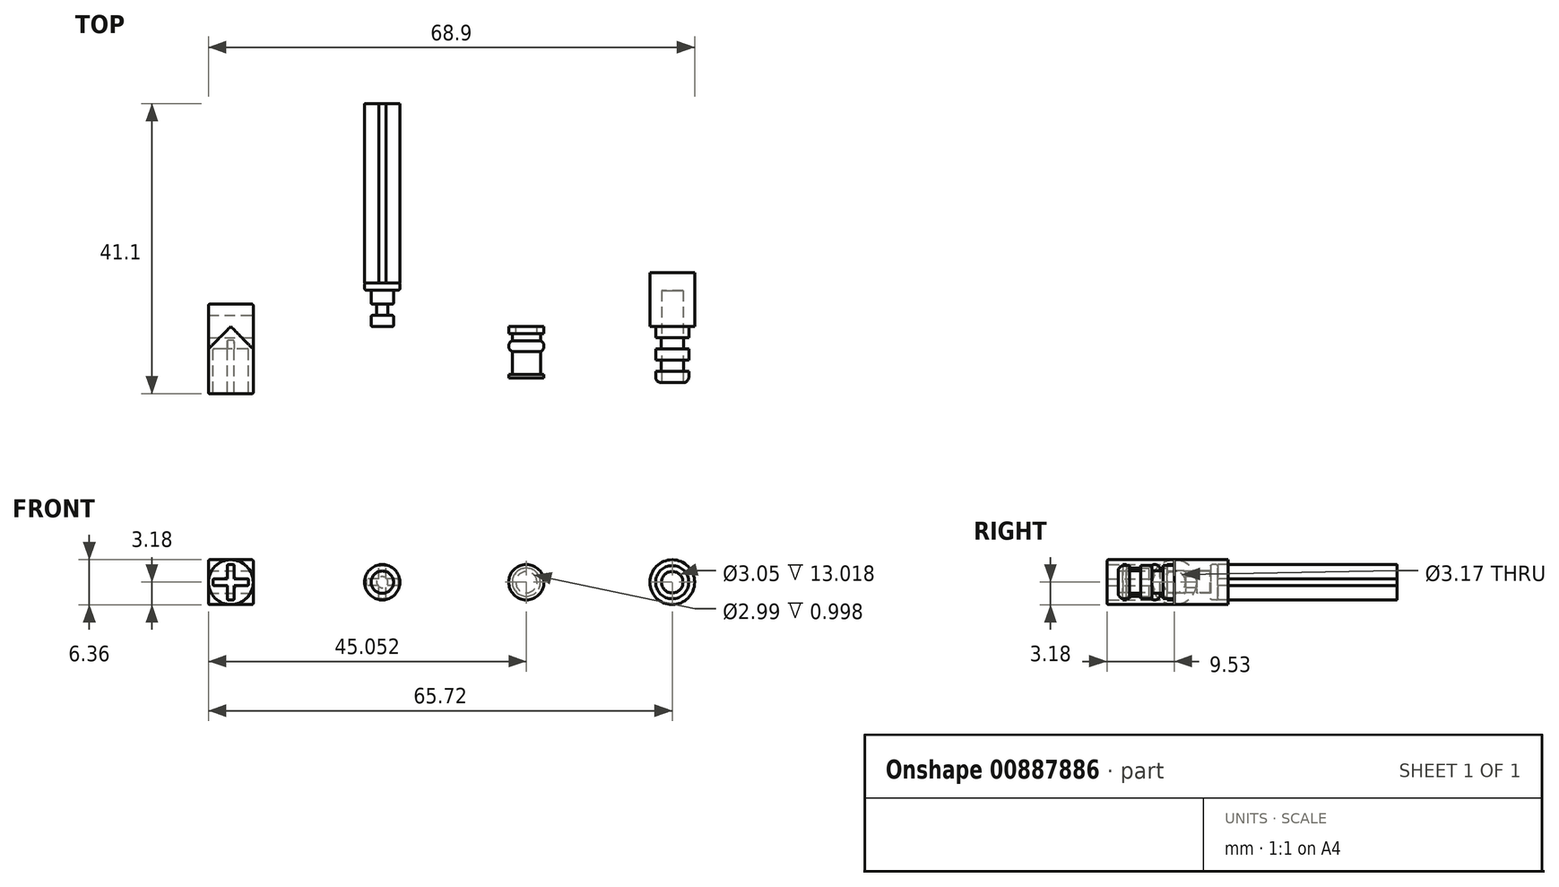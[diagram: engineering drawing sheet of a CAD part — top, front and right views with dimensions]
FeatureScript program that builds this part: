
annotation { "Feature Type Name" : "Feature", "Feature Type Description" : "" }
export const myFeature = defineFeature(function(context is Context, id is Id, definition is map)
    precondition{}
    {
        {
            var Q0;
            Q0=qCreatedBy(makeId("Front.planeOp"),FACE);
            var sketch = newSketch(context, id + "F0", { "sketchPlane" : qUnion([Q0])});
            skCircle(sketch, "E0", {"center": v(-62.55, 0) * mm, "radius": 3.18 * mm});
            skLineSegment(sketch, "E1.bottom", {"start": v(-62.88, 2.5) * mm, "end": v(-62.2, 2.5) * mm});
            skLineSegment(sketch, "E1.top", {"start": v(-62.89, -2.5) * mm, "end": v(-62.2, -2.5) * mm});
            skLineSegment(sketch, "E1.left", {"start": v(-63.05, 2.34) * mm, "end": v(-63.05, -2.34) * mm});
            skLineSegment(sketch, "E1.right", {"start": v(-62.05, 2.34) * mm, "end": v(-62.05, -2.34) * mm});
            skLineSegment(sketch, "E2.bottom", {"start": v(-64.89, 0.5) * mm, "end": v(-60.2, 0.5) * mm});
            skLineSegment(sketch, "E2.top", {"start": v(-64.89, -0.5) * mm, "end": v(-60.2, -0.5) * mm});
            skLineSegment(sketch, "E2.left", {"start": v(-65.05, 0.34) * mm, "end": v(-65.05, -0.34) * mm});
            skLineSegment(sketch, "E2.right", {"start": v(-60.05, 0.34) * mm, "end": v(-60.05, -0.34) * mm});
            skPoint(sketch, "E3.visualSharp", {"position": v(-63.05, 2.5) * mm});
            skArc(sketch, "E3.filletArc", {"start": v(-62.88, 2.5) * mm, "mid": v(-63, 2.45) * mm, "end": v(-63.05, 2.34) * mm});
            skPoint(sketch, "E4.visualSharp", {"position": v(-62.05, 2.5) * mm});
            skArc(sketch, "E4.filletArc", {"start": v(-62.05, 2.34) * mm, "mid": v(-62.1, 2.45) * mm, "end": v(-62.2, 2.5) * mm});
            skPoint(sketch, "E5.visualSharp", {"position": v(-60.05, 0.5) * mm});
            skArc(sketch, "E5.filletArc", {"start": v(-60.05, 0.34) * mm, "mid": v(-60.1, 0.45) * mm, "end": v(-60.2, 0.5) * mm});
            skPoint(sketch, "E6.visualSharp", {"position": v(-60.05, -0.5) * mm});
            skArc(sketch, "E6.filletArc", {"start": v(-60.2, -0.5) * mm, "mid": v(-60.1, -0.45) * mm, "end": v(-60.05, -0.34) * mm});
            skPoint(sketch, "E7.visualSharp", {"position": v(-62.05, -2.5) * mm});
            skArc(sketch, "E7.filletArc", {"start": v(-62.2, -2.5) * mm, "mid": v(-62.1, -2.45) * mm, "end": v(-62.05, -2.34) * mm});
            skPoint(sketch, "E8.visualSharp", {"position": v(-63.05, -2.5) * mm});
            skArc(sketch, "E8.filletArc", {"start": v(-63.05, -2.34) * mm, "mid": v(-63, -2.45) * mm, "end": v(-62.89, -2.5) * mm});
            skPoint(sketch, "E9.visualSharp", {"position": v(-65.05, -0.5) * mm});
            skArc(sketch, "E9.filletArc", {"start": v(-65.05, -0.34) * mm, "mid": v(-65, -0.45) * mm, "end": v(-64.89, -0.5) * mm});
            skPoint(sketch, "E10.visualSharp", {"position": v(-65.05, 0.5) * mm});
            skArc(sketch, "E10.filletArc", {"start": v(-64.89, 0.5) * mm, "mid": v(-65, 0.45) * mm, "end": v(-65.05, 0.34) * mm});
            skLineSegment(sketch, "E11.bottom", {"start": v(-65.72, 3.18) * mm, "end": v(-59.37, 3.18) * mm});
            skLineSegment(sketch, "E11.top", {"start": v(-65.72, 0) * mm, "end": v(-59.37, 0) * mm});
            skLineSegment(sketch, "E11.left", {"start": v(-65.72, 3.18) * mm, "end": v(-65.72, 0) * mm});
            skLineSegment(sketch, "E11.right", {"start": v(-59.37, 3.18) * mm, "end": v(-59.37, 0) * mm});
            skSolve(sketch);
        }
        {
            var Q0;
            Q0=makeQuery(id+"F0.imprint","IMPRINT",FACE,{"disambiguationData":[TD([[makeQuery(id+"F0.imprint","IMPRINT",EDGE,{"derivedFrom":sQuery(id+"F0.wireOp",EDGE,"E1.bottom")}),1.0]])]});
            var Q1;
            Q1=makeQuery(id+"F0.imprint","IMPRINT",FACE,{"disambiguationData":[TD([[makeQuery(id+"F0.imprint","IMPRINT",EDGE,{"derivedFrom":sQuery(id+"F0.wireOp",EDGE,"E1.top")}),-1.0]])]});
            extrude(context, id + "F1", {"entities" : qUnion([Q0, Q1]), "depth" : 9.52 * mm, "offsetDistance" : 25.4 * mm});
        }
        {
            var Q0;
            Q0=makeQuery(id+"F0.imprint","IMPRINT",FACE,{"disambiguationData":[TD([[makeQuery(id+"F0.imprint","IMPRINT",EDGE,{"derivedFrom":sQuery(id+"F0.wireOp",EDGE,"E1.bottom")}),1.0]])]});
            var Q1;
            {var subQ0=sQuery(id+"F0.wireOp",EDGE,"E11.right");Q1=makeQuery(id+"F0.imprint","IMPRINT",FACE,{"disambiguationData":[TD([[makeQuery(id+"F0.imprint","IMPRINT",EDGE,{"derivedFrom":subQ0}),-1.0]])]});}
            var Q2;
            {var subQ0=sQuery(id+"F0.wireOp",EDGE,"E11.left");Q2=makeQuery(id+"F0.imprint","IMPRINT",FACE,{"disambiguationData":[TD([[makeQuery(id+"F0.imprint","IMPRINT",EDGE,{"derivedFrom":subQ0}),1.0]])]});}
            var Q3;
            {var subQ0=sQuery(id+"F0.wireOp",EDGE,"E5.filletArc");Q3=makeQuery(id+"F0.imprint","IMPRINT",FACE,{"disambiguationData":[TD([[makeQuery(id+"F0.imprint","IMPRINT",EDGE,{"derivedFrom":subQ0}),1.0]])]});}
            var Q4;
            {var subQ0=sQuery(id+"F0.wireOp",EDGE,"E2.bottom");var subQ1=sQuery(id+"F0.wireOp",EDGE,"E1.left");var subQ2=makeQuery(id+"F0.imprint","INTERSECT",VERTEX,{"derivedFrom":[subQ1,subQ0]});Q4=makeQuery(id+"F0.imprint","IMPRINT",FACE,{"disambiguationData":[TD([[makeQuery(id+"F0.imprint","IMPRINT",EDGE,{"disambiguationData":[TD([[subQ2,-1.0]])],"derivedFrom":subQ1}),1.0]])]});}
            var Q5;
            {var subQ0=sQuery(id+"F0.wireOp",EDGE,"E10.filletArc");Q5=makeQuery(id+"F0.imprint","IMPRINT",FACE,{"disambiguationData":[TD([[makeQuery(id+"F0.imprint","IMPRINT",EDGE,{"derivedFrom":subQ0}),1.0]])]});}
            var Q6;
            Q6=makeQuery(id+"F0.imprint","IMPRINT",FACE,{"disambiguationData":[TD([[makeQuery(id+"F0.imprint","IMPRINT",EDGE,{"derivedFrom":sQuery(id+"F0.wireOp",EDGE,"E1.bottom")}),-1.0]])]});
            var Q7;
            Q7=sQuery(id+"F0.wireOp",EDGE,"E11.top");
            revolve(context, id + "F2", {"operationType" : NewBodyOperationType.ADD, "surfaceOperationType" : NewSurfaceOperationType.NEW, "entities" : qUnion([Q0, Q1, Q2, Q3, Q4, Q5, Q6]), "axis" : qUnion([Q7]), "revolveType" : RevolveType.FULL});
        }
        {
            var Q0;
            Q0=makeQuery(id+"F2.opRevolve","SWEPT_FACE",FACE,{"disambiguationData":[OSD([sQuery(id+"F0.wireOp",EDGE,"E11.right")])]});
            var sketch = newSketch(context, id + "F3", { "sketchPlane" : qUnion([Q0])});
            skCircle(sketch, "E12", {"center": v(0, 0) * mm, "radius": 1.59 * mm});
            skSolve(sketch);
        }
        {
            var Q0;
            Q0=makeQuery(id+"F3.imprint","IMPRINT",FACE,{"disambiguationData":[TD([[makeQuery(id+"F3.imprint","IMPRINT",EDGE,{"derivedFrom":sQuery(id+"F3.wireOp",EDGE,"E12")}),1.0]])]});
            extrude(context, id + "F4", {"entities" : qUnion([Q0]), "operationType" : NewBodyOperationType.REMOVE, "oppositeDirection" : true, "depth" : 6.35 * mm, "offsetDistance" : 25.4 * mm});
        }
        {
            var Q0;
            Q0=qCreatedBy(makeId("Front.planeOp"),FACE);
            var sketch = newSketch(context, id + "F5", { "sketchPlane" : qUnion([Q0])});
            skCircle(sketch, "E13", {"center": v(-41.08, 0) * mm, "radius": 1.59 * mm});
            skSolve(sketch);
        }
        {
            var Q0;
            Q0=makeQuery(id+"F5.imprint","IMPRINT",FACE,{"disambiguationData":[TD([[makeQuery(id+"F5.imprint","IMPRINT",EDGE,{"derivedFrom":sQuery(id+"F5.wireOp",EDGE,"E13")}),1.0]])]});
            extrude(context, id + "F6", {"entities" : qUnion([Q0]), "depth" : 1.59 * mm, "offsetDistance" : 25.4 * mm});
        }
        {
            var Q0;
            Q0=makeQuery(id+"F6.opExtrude","CAP_FACE",FACE,{"disambiguationData":[OSD([sQuery(id+"F5.wireOp",EDGE,"E13")])],"isStart":false});
            var sketch = newSketch(context, id + "F7", { "sketchPlane" : qUnion([Q0])});
            skCircle(sketch, "E14", {"center": v(-41.08, 0) * mm, "radius": 0.8 * mm});
            skSolve(sketch);
        }
        {
            var Q0;
            Q0=makeQuery(id+"F7.imprint","IMPRINT",FACE,{"disambiguationData":[TD([[makeQuery(id+"F7.imprint","IMPRINT",EDGE,{"derivedFrom":sQuery(id+"F7.wireOp",EDGE,"E14")}),1.0]])]});
            extrude(context, id + "F8", {"entities" : qUnion([Q0]), "operationType" : NewBodyOperationType.ADD, "depth" : 1.59 * mm, "offsetDistance" : 25.4 * mm});
        }
        {
            var Q0;
            Q0=makeQuery(id+"F8.opExtrude","CAP_FACE",FACE,{"disambiguationData":[OSD([sQuery(id+"F7.wireOp",EDGE,"E14")])],"isStart":false});
            var sketch = newSketch(context, id + "F9", { "sketchPlane" : qUnion([Q0])});
            skCircle(sketch, "E15", {"center": v(-41.08, 0) * mm, "radius": 1.59 * mm});
            skSolve(sketch);
        }
        {
            var Q0;
            Q0=makeQuery(id+"F9.imprint","IMPRINT",FACE,{"disambiguationData":[TD([[makeQuery(id+"F9.imprint","IMPRINT",EDGE,{"derivedFrom":makeQuery(id+"F8.opExtrude","CAP_EDGE",EDGE,{"disambiguationData":[OSD([sQuery(id+"F7.wireOp",EDGE,"E14")])],"isStart":false})}),1.0]])]});
            var Q1;
            Q1=makeQuery(id+"F9.imprint","IMPRINT",FACE,{"disambiguationData":[TD([[makeQuery(id+"F9.imprint","IMPRINT",EDGE,{"derivedFrom":sQuery(id+"F9.wireOp",EDGE,"E15")}),1.0]])]});
            extrude(context, id + "F10", {"entities" : qUnion([Q0, Q1]), "operationType" : NewBodyOperationType.ADD, "depth" : 2 * mm, "offsetDistance" : 25.4 * mm});
        }
        {
            var Q0;
            Q0=makeQuery(id+"F10.opExtrude","CAP_FACE",FACE,{"disambiguationData":[OSD([sQuery(id+"F9.wireOp",EDGE,"E15")])],"isStart":false});
            var sketch = newSketch(context, id + "F11", { "sketchPlane" : qUnion([Q0])});
            skCircle(sketch, "E16", {"center": v(-41.08, 0) * mm, "radius": 2.5 * mm});
            skSolve(sketch);
        }
        {
            var Q0;
            Q0=makeQuery(id+"F11.imprint","IMPRINT",FACE,{"disambiguationData":[TD([[makeQuery(id+"F11.imprint","IMPRINT",EDGE,{"derivedFrom":makeQuery(id+"F10.opExtrude","CAP_EDGE",EDGE,{"disambiguationData":[OSD([sQuery(id+"F9.wireOp",EDGE,"E15")])],"isStart":false})}),1.0]])]});
            var Q1;
            Q1=makeQuery(id+"F11.imprint","IMPRINT",FACE,{"disambiguationData":[TD([[makeQuery(id+"F11.imprint","IMPRINT",EDGE,{"derivedFrom":sQuery(id+"F11.wireOp",EDGE,"E16")}),1.0]])]});
            extrude(context, id + "F12", {"entities" : qUnion([Q0, Q1]), "operationType" : NewBodyOperationType.ADD, "depth" : 1 * mm, "offsetDistance" : 25.4 * mm});
        }
        {
            var Q0;
            Q0=makeQuery(id+"F1.opExtrude","CAP_EDGE",EDGE,{"disambiguationData":[OSD([sQuery(id+"F0.wireOp",EDGE,"E0")])],"isStart":false});
            var Q1;
            Q1=makeQuery(id+"F2.opRevolve","SWEPT_EDGE",EDGE,{"disambiguationData":[OSD([sQuery(id+"F0.wireOp",EDGE,"E11.bottom"),sQuery(id+"F0.wireOp",EDGE,"E11.right")])]});
            var Q2;
            Q2=makeQuery(id+"F2.opRevolve","SWEPT_EDGE",EDGE,{"disambiguationData":[OSD([sQuery(id+"F0.wireOp",EDGE,"E11.bottom"),sQuery(id+"F0.wireOp",EDGE,"E11.left")])]});
            var Q3;
            Q3=makeQuery(id+"F6.opExtrude","CAP_EDGE",EDGE,{"disambiguationData":[OSD([sQuery(id+"F5.wireOp",EDGE,"E13")])],"isStart":true});
            var Q4;
            Q4=makeQuery(id+"F6.opExtrude","CAP_EDGE",EDGE,{"disambiguationData":[OSD([sQuery(id+"F5.wireOp",EDGE,"E13")])],"isStart":false});
            var Q5;
            Q5=makeQuery(id+"F4.boolean.opBoolean","COPY",EDGE,{"derivedFrom":makeQuery(id+"F4.opExtrude","CAP_EDGE",EDGE,{"disambiguationData":[OSD([sQuery(id+"F3.wireOp",EDGE,"E12")])],"isStart":true})});
            var Q6;
            Q6=makeQuery(id+"F4.boolean.opBoolean","COPY",EDGE,{"derivedFrom":makeQuery(id+"F4.opExtrude","CAP_EDGE",EDGE,{"disambiguationData":[OSD([sQuery(id+"F3.wireOp",EDGE,"E12")])],"isStart":false})});
            var Q7;
            Q7=makeQuery(id+"F1.opExtrude","CAP_FACE",FACE,{"disambiguationData":[OSD([sQuery(id+"F0.wireOp",EDGE,"E0"),sQuery(id+"F0.wireOp",EDGE,"E1.bottom"),sQuery(id+"F0.wireOp",EDGE,"E1.top"),sQuery(id+"F0.wireOp",EDGE,"E1.left"),sQuery(id+"F0.wireOp",EDGE,"E1.right"),sQuery(id+"F0.wireOp",EDGE,"E2.bottom"),sQuery(id+"F0.wireOp",EDGE,"E2.top"),sQuery(id+"F0.wireOp",EDGE,"E2.left"),sQuery(id+"F0.wireOp",EDGE,"E2.right"),sQuery(id+"F0.wireOp",EDGE,"E3.filletArc"),sQuery(id+"F0.wireOp",EDGE,"E4.filletArc"),sQuery(id+"F0.wireOp",EDGE,"E5.filletArc"),sQuery(id+"F0.wireOp",EDGE,"E6.filletArc"),sQuery(id+"F0.wireOp",EDGE,"E7.filletArc"),sQuery(id+"F0.wireOp",EDGE,"E8.filletArc"),sQuery(id+"F0.wireOp",EDGE,"E9.filletArc"),sQuery(id+"F0.wireOp",EDGE,"E10.filletArc")])],"isStart":false});
            var Q8;
            Q8=makeQuery(id+"F10.opExtrude","CAP_EDGE",EDGE,{"disambiguationData":[OSD([sQuery(id+"F9.wireOp",EDGE,"E15")])],"isStart":true});
            var Q9;
            Q9=makeQuery(id+"F10.opExtrude","CAP_EDGE",EDGE,{"disambiguationData":[OSD([sQuery(id+"F9.wireOp",EDGE,"E15")])],"isStart":false});
            var Q10;
            Q10=makeQuery(id+"F12.opExtrude","CAP_EDGE",EDGE,{"disambiguationData":[OSD([sQuery(id+"F11.wireOp",EDGE,"E16")])],"isStart":true});
            var Q11;
            Q11=makeQuery(id+"F12.opExtrude","CAP_EDGE",EDGE,{"disambiguationData":[OSD([sQuery(id+"F11.wireOp",EDGE,"E16")])],"isStart":false});
            fillet(context, id + "F13", {"entities" : qUnion([Q0, Q1, Q2, Q3, Q4, Q5, Q6, Q7, Q8, Q9, Q10, Q11]), "radius" : 0.2 * mm, "tangentPropagation" : true, "allowEdgeOverflow" : false});
        }
        {
            var Q0;
            Q0=makeQuery(id+"F12.opExtrude","CAP_FACE",FACE,{"disambiguationData":[OSD([sQuery(id+"F11.wireOp",EDGE,"E16")])],"isStart":false});
            var sketch = newSketch(context, id + "F14", { "sketchPlane" : qUnion([Q0])});
            skLineSegment(sketch, "E17.bottom", {"start": v(-40.74, 2.5) * mm, "end": v(-41.42, 2.5) * mm});
            skLineSegment(sketch, "E17.top", {"start": v(-40.74, -2.5) * mm, "end": v(-41.42, -2.5) * mm});
            skLineSegment(sketch, "E17.left", {"start": v(-40.58, 2.34) * mm, "end": v(-40.58, -2.34) * mm});
            skLineSegment(sketch, "E17.right", {"start": v(-41.58, 2.34) * mm, "end": v(-41.58, -2.34) * mm});
            skPoint(sketch, "E17.middle", {"position": v(-41.08, 0) * mm});
            skLineSegment(sketch, "E18.bottom", {"start": v(-38.74, 0.5) * mm, "end": v(-43.41, 0.5) * mm});
            skLineSegment(sketch, "E18.top", {"start": v(-38.74, -0.5) * mm, "end": v(-43.41, -0.5) * mm});
            skLineSegment(sketch, "E18.left", {"start": v(-38.58, 0.34) * mm, "end": v(-38.58, -0.34) * mm});
            skLineSegment(sketch, "E18.right", {"start": v(-43.57, 0.34) * mm, "end": v(-43.57, -0.34) * mm});
            skPoint(sketch, "E19.visualSharp", {"position": v(-41.58, 2.5) * mm});
            skArc(sketch, "E19.filletArc", {"start": v(-41.42, 2.5) * mm, "mid": v(-41.53, 2.45) * mm, "end": v(-41.58, 2.34) * mm});
            skPoint(sketch, "E20.visualSharp", {"position": v(-40.58, 2.5) * mm});
            skArc(sketch, "E20.filletArc", {"start": v(-40.58, 2.34) * mm, "mid": v(-40.62, 2.45) * mm, "end": v(-40.74, 2.5) * mm});
            skPoint(sketch, "E21.visualSharp", {"position": v(-38.58, 0.5) * mm});
            skArc(sketch, "E21.filletArc", {"start": v(-38.58, 0.34) * mm, "mid": v(-38.63, 0.45) * mm, "end": v(-38.74, 0.5) * mm});
            skPoint(sketch, "E22.visualSharp", {"position": v(-38.58, -0.5) * mm});
            skArc(sketch, "E22.filletArc", {"start": v(-38.74, -0.5) * mm, "mid": v(-38.63, -0.45) * mm, "end": v(-38.58, -0.34) * mm});
            skPoint(sketch, "E23.visualSharp", {"position": v(-40.58, -2.5) * mm});
            skArc(sketch, "E23.filletArc", {"start": v(-40.74, -2.5) * mm, "mid": v(-40.62, -2.45) * mm, "end": v(-40.58, -2.34) * mm});
            skPoint(sketch, "E24.visualSharp", {"position": v(-41.58, -2.5) * mm});
            skArc(sketch, "E24.filletArc", {"start": v(-41.58, -2.34) * mm, "mid": v(-41.53, -2.45) * mm, "end": v(-41.42, -2.5) * mm});
            skPoint(sketch, "E25.visualSharp", {"position": v(-43.57, 0.5) * mm});
            skArc(sketch, "E25.filletArc", {"start": v(-43.41, 0.5) * mm, "mid": v(-43.53, 0.45) * mm, "end": v(-43.57, 0.34) * mm});
            skPoint(sketch, "E26.visualSharp", {"position": v(-43.57, -0.5) * mm});
            skArc(sketch, "E26.filletArc", {"start": v(-43.57, -0.34) * mm, "mid": v(-43.53, -0.45) * mm, "end": v(-43.41, -0.5) * mm});
            skSolve(sketch);
        }
        {
            var Q0;
            Q0=makeQuery(id+"F14.imprint","IMPRINT",FACE,{"disambiguationData":[TD([[makeQuery(id+"F14.imprint","IMPRINT",EDGE,{"derivedFrom":sQuery(id+"F14.wireOp",EDGE,"E17.bottom")}),1.0]])]});
            var Q1;
            Q1=makeQuery(id+"F14.imprint","IMPRINT",FACE,{"disambiguationData":[TD([[makeQuery(id+"F14.imprint","IMPRINT",EDGE,{"derivedFrom":sQuery(id+"F14.wireOp",EDGE,"E18.left")}),-1.0]])]});
            var Q2;
            Q2=makeQuery(id+"F14.imprint","IMPRINT",FACE,{"disambiguationData":[TD([[makeQuery(id+"F14.imprint","IMPRINT",EDGE,{"derivedFrom":sQuery(id+"F14.wireOp",EDGE,"E17.top")}),-1.0]])]});
            var Q3;
            {var subQ0=sQuery(id+"F14.wireOp",EDGE,"E18.bottom");var subQ1=sQuery(id+"F14.wireOp",EDGE,"E17.left");var subQ2=makeQuery(id+"F14.imprint","INTERSECT",VERTEX,{"derivedFrom":[subQ1,subQ0]});Q3=makeQuery(id+"F14.imprint","IMPRINT",FACE,{"disambiguationData":[TD([[makeQuery(id+"F14.imprint","IMPRINT",EDGE,{"disambiguationData":[TD([[subQ2,-1.0]])],"derivedFrom":subQ1}),1.0]])]});}
            var Q4;
            {var subQ0=sQuery(id+"F14.wireOp",EDGE,"E18.bottom");var subQ1=sQuery(id+"F14.wireOp",EDGE,"E17.left");var subQ2=makeQuery(id+"F14.imprint","INTERSECT",VERTEX,{"derivedFrom":[subQ1,subQ0]});Q4=makeQuery(id+"F14.imprint","IMPRINT",FACE,{"disambiguationData":[TD([[makeQuery(id+"F14.imprint","IMPRINT",EDGE,{"disambiguationData":[TD([[subQ2,-1.0]])],"derivedFrom":subQ1}),-1.0]])]});}
            var Q5;
            {var subQ0=sQuery(id+"F14.wireOp",EDGE,"E18.bottom");var subQ1=sQuery(id+"F14.wireOp",EDGE,"E17.left");var subQ2=makeQuery(id+"F14.imprint","INTERSECT",VERTEX,{"derivedFrom":[subQ1,subQ0]});Q5=makeQuery(id+"F14.imprint","IMPRINT",FACE,{"disambiguationData":[TD([[makeQuery(id+"F14.imprint","IMPRINT",EDGE,{"disambiguationData":[TD([[subQ2,-1.0]])],"derivedFrom":subQ0}),-1.0]])]});}
            var Q6;
            {var subQ0=sQuery(id+"F14.wireOp",EDGE,"E18.top");var subQ1=sQuery(id+"F14.wireOp",EDGE,"E17.left");var subQ2=makeQuery(id+"F14.imprint","INTERSECT",VERTEX,{"derivedFrom":[subQ1,subQ0]});Q6=makeQuery(id+"F14.imprint","IMPRINT",FACE,{"disambiguationData":[TD([[makeQuery(id+"F14.imprint","IMPRINT",EDGE,{"disambiguationData":[TD([[subQ2,-1.0]])],"derivedFrom":subQ0}),1.0]])]});}
            var Q7;
            Q7=makeQuery(id+"F14.imprint","IMPRINT",FACE,{"disambiguationData":[TD([[makeQuery(id+"F14.imprint","IMPRINT",EDGE,{"derivedFrom":sQuery(id+"F14.wireOp",EDGE,"E18.right")}),1.0]])]});
            var Q8;
            {var subQ0=sQuery(id+"F14.wireOp",EDGE,"E18.bottom");var subQ1=sQuery(id+"F14.wireOp",EDGE,"E17.right");var subQ2=makeQuery(id+"F14.imprint","INTERSECT",VERTEX,{"derivedFrom":[subQ1,subQ0]});Q8=makeQuery(id+"F14.imprint","IMPRINT",FACE,{"disambiguationData":[TD([[makeQuery(id+"F14.imprint","IMPRINT",EDGE,{"disambiguationData":[TD([[subQ2,-1.0]])],"derivedFrom":subQ1}),-1.0]])]});}
            extrude(context, id + "F15", {"entities" : qUnion([Q0, Q1, Q2, Q3, Q4, Q5, Q6, Q7, Q8]), "operationType" : NewBodyOperationType.ADD, "depth" : 25.4 * mm, "offsetDistance" : 25.4 * mm});
        }
        {
            var Q0;
            Q0=makeQuery(id+"F6.opExtrude","SWEPT_BODY",BODY,{"disambiguationData":[OSD([sQuery(id+"F5.wireOp",EDGE,"E13")])]});
            var Q1;
            Q1=makeQuery(id+"F4.boolean.opBoolean","COPY",FACE,{"derivedFrom":makeQuery(id+"F4.opExtrude","SWEPT_FACE",FACE,{"disambiguationData":[OSD([sQuery(id+"F3.wireOp",EDGE,"E12")])]})});
            transform(context, id + "F16", {"entities" : qUnion([Q0]), "transformType" : TransformType.ROTATION, "transformAxis" : qUnion([Q1]), "angle" : 180 * degree, "makeCopy" : false});
        }
        {
            var Q0;
            Q0=qCreatedBy(makeId("Front.planeOp"),FACE);
            var sketch = newSketch(context, id + "F17", { "sketchPlane" : qUnion([Q0])});
            skCircle(sketch, "E27", {"center": v(-20.67, 0) * mm, "radius": 2.5 * mm});
            skCircle(sketch, "E28", {"center": v(-20.67, 0) * mm, "radius": 1.5 * mm});
            skSolve(sketch);
        }
        {
            var Q0;
            Q0 = qSketchRegion(id + "F17", true);
            extrude(context, id + "F18", {"entities" : qUnion([Q0]), "depth" : 1 * mm, "offsetDistance" : 25.4 * mm});
        }
        {
            var Q0;
            Q0=makeQuery(id+"F18.opExtrude","CAP_FACE",FACE,{"disambiguationData":[OSD([sQuery(id+"F17.wireOp",EDGE,"E27")])],"isStart":false});
            var sketch = newSketch(context, id + "F19", { "sketchPlane" : qUnion([Q0])});
            skCircle(sketch, "E29", {"center": v(-20.67, 0) * mm, "radius": 2 * mm});
            skSolve(sketch);
        }
        {
            var Q0;
            Q0 = qSketchRegion(id + "F19", true);
            extrude(context, id + "F20", {"entities" : qUnion([Q0]), "operationType" : NewBodyOperationType.ADD, "depth" : 1 * mm, "offsetDistance" : 25.4 * mm});
        }
        {
            var Q0;
            Q0=makeQuery(id+"F20.opExtrude","CAP_FACE",FACE,{"disambiguationData":[OSD([sQuery(id+"F19.wireOp",EDGE,"E29")])],"isStart":false});
            var sketch = newSketch(context, id + "F21", { "sketchPlane" : qUnion([Q0])});
            skCircle(sketch, "E30", {"center": v(-20.67, 0) * mm, "radius": 2.5 * mm});
            skSolve(sketch);
        }
        {
            var Q0;
            Q0 = qSketchRegion(id + "F21", true);
            extrude(context, id + "F22", {"entities" : qUnion([Q0]), "operationType" : NewBodyOperationType.ADD, "depth" : 1.59 * mm, "offsetDistance" : 25.4 * mm});
        }
        {
            var Q0;
            Q0=makeQuery(id+"F22.opExtrude","CAP_EDGE",EDGE,{"disambiguationData":[OSD([sQuery(id+"F21.wireOp",EDGE,"E30")])],"isStart":true});
            var Q1;
            Q1=makeQuery(id+"F22.opExtrude","CAP_EDGE",EDGE,{"disambiguationData":[OSD([sQuery(id+"F21.wireOp",EDGE,"E30")])],"isStart":false});
            fillet(context, id + "F23", {"entities" : qUnion([Q0, Q1]), "radius" : 0.8 * mm, "tangentPropagation" : true, "allowEdgeOverflow" : false});
        }
        {
            var Q0;
            Q0=makeQuery(id+"F22.opExtrude","CAP_FACE",FACE,{"disambiguationData":[OSD([sQuery(id+"F21.wireOp",EDGE,"E30")])],"isStart":false});
            var sketch = newSketch(context, id + "F24", { "sketchPlane" : qUnion([Q0])});
            skCircle(sketch, "E31", {"center": v(-20.67, 0) * mm, "radius": 2 * mm});
            skSolve(sketch);
        }
        {
            var Q0;
            Q0=makeQuery(id+"F24.imprint","IMPRINT",FACE,{"disambiguationData":[TD([[makeQuery(id+"F24.imprint","IMPRINT",EDGE,{"derivedFrom":sQuery(id+"F24.wireOp",EDGE,"E31")}),1.0]])]});
            var Q1;
            {var subQ0=sQuery(id+"F21.wireOp",EDGE,"E30");Q1=makeQuery(id+"F24.imprint","IMPRINT",FACE,{"disambiguationData":[TD([[makeQuery(id+"F24.imprint","IMPRINT",EDGE,{"derivedFrom":makeQuery(id+"F23.opFillet","BLEND_EDGE",EDGE,{"blendedFrom":[makeQuery(id+"F22.opExtrude","CAP_EDGE",EDGE,{"disambiguationData":[OSD([subQ0])],"isStart":false}),makeQuery(id+"F22.opExtrude","CAP_FACE",FACE,{"disambiguationData":[OSD([subQ0])],"isStart":false})],"blendedInto":[makeQuery(id+"F22.opExtrude","CAP_FACE",FACE,{"disambiguationData":[OSD([subQ0])],"isStart":false})]})}),1.0]])]});}
            extrude(context, id + "F25", {"entities" : qUnion([Q0, Q1]), "operationType" : NewBodyOperationType.ADD, "depth" : 3.17 * mm, "offsetDistance" : 25.4 * mm, "hasSecondDirection" : true, "secondDirectionOppositeDirection" : true, "secondDirectionDepth" : 2.54 * mm});
        }
        {
            var Q0;
            Q0=makeQuery(id+"F25.opExtrude","CAP_FACE",FACE,{"disambiguationData":[OSD([sQuery(id+"F24.wireOp",EDGE,"E31")])],"isStart":false});
            var sketch = newSketch(context, id + "F26", { "sketchPlane" : qUnion([Q0])});
            skCircle(sketch, "E32", {"center": v(-20.67, 0) * mm, "radius": 2.5 * mm});
            skSolve(sketch);
        }
        {
            var Q0;
            Q0=makeQuery(id+"F26.imprint","IMPRINT",FACE,{"disambiguationData":[TD([[makeQuery(id+"F26.imprint","IMPRINT",EDGE,{"derivedFrom":sQuery(id+"F26.wireOp",EDGE,"E32")}),1.0]])]});
            var Q1;
            Q1=makeQuery(id+"F26.imprint","IMPRINT",FACE,{"disambiguationData":[TD([[makeQuery(id+"F26.imprint","IMPRINT",EDGE,{"derivedFrom":makeQuery(id+"F25.opExtrude","CAP_EDGE",EDGE,{"disambiguationData":[OSD([sQuery(id+"F24.wireOp",EDGE,"E31")])],"isStart":false})}),1.0]])]});
            extrude(context, id + "F27", {"entities" : qUnion([Q0, Q1]), "operationType" : NewBodyOperationType.ADD, "depth" : 0.5 * mm, "offsetDistance" : 25.4 * mm});
        }
        {
            var Q0;
            Q0=qCreatedBy(makeId("Front.planeOp"),FACE);
            var sketch = newSketch(context, id + "F28", { "sketchPlane" : qUnion([Q0])});
            skCircle(sketch, "E33", {"center": v(0, 0) * mm, "radius": 2.35 * mm});
            skSolve(sketch);
        }
        {
            var Q0;
            Q0=makeQuery(id+"F28.imprint","IMPRINT",FACE,{"disambiguationData":[TD([[makeQuery(id+"F28.imprint","IMPRINT",EDGE,{"derivedFrom":sQuery(id+"F28.wireOp",EDGE,"E33")}),1.0]])]});
            extrude(context, id + "F29", {"entities" : qUnion([Q0]), "depth" : 1.59 * mm, "offsetDistance" : 25.4 * mm});
        }
        {
            var Q0;
            Q0=makeQuery(id+"F29.opExtrude","CAP_FACE",FACE,{"disambiguationData":[OSD([sQuery(id+"F28.wireOp",EDGE,"E33"),sQuery(id+"F28.wireOp",EDGE,"9ddfb91d-996f-495a-b1ff-16b5f034c826")])],"isStart":false});
            var sketch = newSketch(context, id + "F30", { "sketchPlane" : qUnion([Q0])});
            skCircle(sketch, "E34", {"center": v(0, 0) * mm, "radius": 1.59 * mm});
            skSolve(sketch);
        }
        {
            var Q0;
            Q0=makeQuery(id+"F30.imprint","IMPRINT",FACE,{"disambiguationData":[TD([[makeQuery(id+"F30.imprint","IMPRINT",EDGE,{"derivedFrom":sQuery(id+"F30.wireOp",EDGE,"E34")}),1.0]])]});
            extrude(context, id + "F31", {"entities" : qUnion([Q0]), "operationType" : NewBodyOperationType.ADD, "depth" : 1.59 * mm, "offsetDistance" : 25.4 * mm});
        }
        {
            var Q0;
            Q0=makeQuery(id+"F31.opExtrude","CAP_FACE",FACE,{"disambiguationData":[OSD([sQuery(id+"F30.wireOp",EDGE,"E34")])],"isStart":false});
            var sketch = newSketch(context, id + "F32", { "sketchPlane" : qUnion([Q0])});
            skCircle(sketch, "E35", {"center": v(0, 0) * mm, "radius": 2.35 * mm});
            skSolve(sketch);
        }
        {
            var Q0;
            Q0=makeQuery(id+"F32.imprint","IMPRINT",FACE,{"disambiguationData":[TD([[makeQuery(id+"F32.imprint","IMPRINT",EDGE,{"derivedFrom":makeQuery(id+"F31.opExtrude","CAP_EDGE",EDGE,{"disambiguationData":[OSD([sQuery(id+"F30.wireOp",EDGE,"E34")])],"isStart":false})}),1.0]])]});
            var Q1;
            Q1=makeQuery(id+"F32.imprint","IMPRINT",FACE,{"disambiguationData":[TD([[makeQuery(id+"F32.imprint","IMPRINT",EDGE,{"derivedFrom":sQuery(id+"F32.wireOp",EDGE,"E35")}),1.0]])]});
            extrude(context, id + "F33", {"entities" : qUnion([Q0, Q1]), "operationType" : NewBodyOperationType.ADD, "depth" : 1.59 * mm, "offsetDistance" : 25.4 * mm});
        }
        {
            var Q0;
            Q0=makeQuery(id+"F33.opExtrude","CAP_FACE",FACE,{"disambiguationData":[OSD([sQuery(id+"F32.wireOp",EDGE,"E35")])],"isStart":false});
            var sketch = newSketch(context, id + "F34", { "sketchPlane" : qUnion([Q0])});
            skCircle(sketch, "E36", {"center": v(0, 0) * mm, "radius": 1.59 * mm});
            skSolve(sketch);
        }
        {
            var Q0;
            Q0=makeQuery(id+"F34.imprint","IMPRINT",FACE,{"disambiguationData":[TD([[makeQuery(id+"F34.imprint","IMPRINT",EDGE,{"derivedFrom":sQuery(id+"F34.wireOp",EDGE,"E36")}),1.0]])]});
            extrude(context, id + "F35", {"entities" : qUnion([Q0]), "operationType" : NewBodyOperationType.ADD, "depth" : 1.59 * mm, "offsetDistance" : 25.4 * mm});
        }
        {
            var Q0;
            Q0=makeQuery(id+"F35.opExtrude","CAP_FACE",FACE,{"disambiguationData":[OSD([sQuery(id+"F34.wireOp",EDGE,"E36")])],"isStart":false});
            var sketch = newSketch(context, id + "F36", { "sketchPlane" : qUnion([Q0])});
            skCircle(sketch, "E37", {"center": v(0, 0) * mm, "radius": 2.35 * mm});
            skSolve(sketch);
        }
        {
            var Q0;
            Q0=makeQuery(id+"F36.imprint","IMPRINT",FACE,{"disambiguationData":[TD([[makeQuery(id+"F36.imprint","IMPRINT",EDGE,{"derivedFrom":makeQuery(id+"F35.opExtrude","CAP_EDGE",EDGE,{"disambiguationData":[OSD([sQuery(id+"F34.wireOp",EDGE,"E36")])],"isStart":false})}),1.0]])]});
            var Q1;
            Q1=makeQuery(id+"F36.imprint","IMPRINT",FACE,{"disambiguationData":[TD([[makeQuery(id+"F36.imprint","IMPRINT",EDGE,{"derivedFrom":sQuery(id+"F36.wireOp",EDGE,"E37")}),1.0]])]});
            extrude(context, id + "F37", {"entities" : qUnion([Q0, Q1]), "operationType" : NewBodyOperationType.ADD, "depth" : 1.59 * mm, "offsetDistance" : 25.4 * mm});
        }
        {
            var Q0;
            Q0=makeQuery(id+"F37.opExtrude","CAP_FACE",FACE,{"disambiguationData":[OSD([sQuery(id+"F36.wireOp",EDGE,"E37")])],"isStart":false});
            var sketch = newSketch(context, id + "F38", { "sketchPlane" : qUnion([Q0])});
            skCircle(sketch, "E38", {"center": v(0, 0) * mm, "radius": 1.52 * mm});
            skSolve(sketch);
        }
        {
            var Q0;
            Q0=makeQuery(id+"F38.imprint","IMPRINT",FACE,{"disambiguationData":[TD([[makeQuery(id+"F38.imprint","IMPRINT",EDGE,{"derivedFrom":sQuery(id+"F38.wireOp",EDGE,"E38")}),1.0]])]});
            extrude(context, id + "F39", {"entities" : qUnion([Q0]), "operationType" : NewBodyOperationType.REMOVE, "oppositeDirection" : true, "depth" : 7.94 * mm, "offsetDistance" : 25.4 * mm});
        }
        {
            var Q0;
            Q0=makeQuery(id+"F37.opExtrude","CAP_EDGE",EDGE,{"disambiguationData":[OSD([sQuery(id+"F36.wireOp",EDGE,"E37")])],"isStart":false});
            var Q1;
            Q1=makeQuery(id+"F35.opExtrude","CAP_EDGE",EDGE,{"disambiguationData":[OSD([sQuery(id+"F34.wireOp",EDGE,"E36")])],"isStart":false});
            var Q2;
            Q2=makeQuery(id+"F35.opExtrude","CAP_EDGE",EDGE,{"disambiguationData":[OSD([sQuery(id+"F34.wireOp",EDGE,"E36")])],"isStart":true});
            var Q3;
            Q3=makeQuery(id+"F31.opExtrude","CAP_EDGE",EDGE,{"disambiguationData":[OSD([sQuery(id+"F30.wireOp",EDGE,"E34")])],"isStart":false});
            var Q4;
            Q4=makeQuery(id+"F31.opExtrude","CAP_EDGE",EDGE,{"disambiguationData":[OSD([sQuery(id+"F30.wireOp",EDGE,"E34")])],"isStart":true});
            fillet(context, id + "F40", {"entities" : qUnion([Q0, Q1, Q2, Q3, Q4]), "radius" : 0.8 * mm, "tangentPropagation" : true, "allowEdgeOverflow" : false});
        }
        {
            var Q0;
            Q0=makeQuery(id+"F29.opExtrude","CAP_FACE",FACE,{"disambiguationData":[OSD([sQuery(id+"F28.wireOp",EDGE,"E33")])],"isStart":true});
            var sketch = newSketch(context, id + "F41", { "sketchPlane" : qUnion([Q0])});
            skCircle(sketch, "E39", {"center": v(0, 0) * mm, "radius": 3.18 * mm});
            skSolve(sketch);
        }
        {
            var Q0;
            Q0=makeQuery(id+"F41.imprint","IMPRINT",FACE,{"disambiguationData":[TD([[makeQuery(id+"F41.imprint","IMPRINT",EDGE,{"derivedFrom":makeQuery(id+"F29.opExtrude","CAP_EDGE",EDGE,{"disambiguationData":[OSD([sQuery(id+"F28.wireOp",EDGE,"E33")])],"isStart":true})}),-1.0]])]});
            var Q1;
            Q1=makeQuery(id+"F41.imprint","IMPRINT",FACE,{"disambiguationData":[TD([[makeQuery(id+"F41.imprint","IMPRINT",EDGE,{"derivedFrom":sQuery(id+"F41.wireOp",EDGE,"E39")}),1.0]])]});
            extrude(context, id + "F42", {"entities" : qUnion([Q0, Q1]), "operationType" : NewBodyOperationType.ADD, "depth" : 5.08 * mm, "offsetDistance" : 25.4 * mm});
        }
        {
            var Q0;
            Q0=makeQuery(id+"F42.opExtrude","CAP_FACE",FACE,{"disambiguationData":[OSD([sQuery(id+"F38.wireOp",EDGE,"E38"),sQuery(id+"F41.wireOp",EDGE,"E39")])],"isStart":false});
            var sketch = newSketch(context, id + "F43", { "sketchPlane" : qUnion([Q0])});
            skCircle(sketch, "E40", {"center": v(0, 0) * mm, "radius": 3.18 * mm});
            skSolve(sketch);
        }
        {
            var Q0;
            Q0=makeQuery(id+"F43.imprint","IMPRINT",FACE,{"disambiguationData":[TD([[makeQuery(id+"F43.imprint","IMPRINT",EDGE,{"derivedFrom":makeQuery(id+"F42.opExtrude","CAP_EDGE",EDGE,{"disambiguationData":[OSD([sQuery(id+"F38.wireOp",EDGE,"E38")])],"isStart":false})}),-1.0]])]});
            var Q1;
            Q1=makeQuery(id+"F43.imprint","IMPRINT",FACE,{"disambiguationData":[TD([[makeQuery(id+"F43.imprint","IMPRINT",EDGE,{"derivedFrom":sQuery(id+"F43.wireOp",EDGE,"E40")}),1.0]])]});
            extrude(context, id + "F44", {"entities" : qUnion([Q0, Q1]), "operationType" : NewBodyOperationType.ADD, "depth" : 2.54 * mm, "offsetDistance" : 25.4 * mm});
        }
    });
